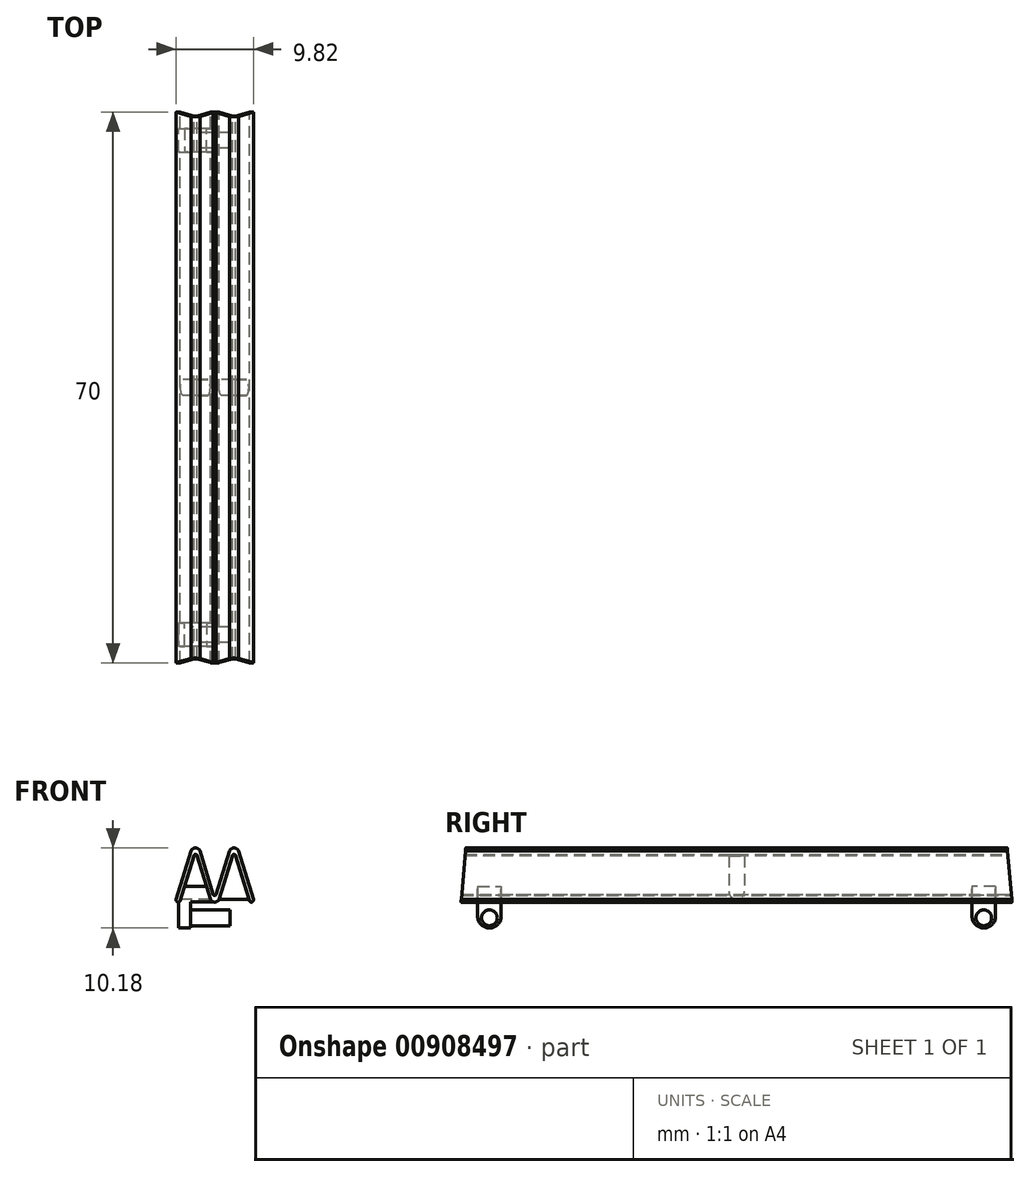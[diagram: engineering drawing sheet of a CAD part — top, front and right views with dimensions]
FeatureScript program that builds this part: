
annotation { "Feature Type Name" : "Feature", "Feature Type Description" : "" }
export const myFeature = defineFeature(function(context is Context, id is Id, definition is map)
    precondition{}
    {
        {
            var Q0;
            Q0=qCreatedBy(makeId("Front.planeOp"),FACE);
            var sketch = newSketch(context, id + "F0", { "sketchPlane" : qUnion([Q0])});
            skLineSegment(sketch, "E0.MirrorCS", {"start": v(6, 0) * mm, "end": v(-6, 0) * mm, "construction": true});
            skLineSegment(sketch, "E1", {"start": v(-6, 9.34) * mm, "end": v(-6, 0) * mm, "construction": true});
            skLineSegment(sketch, "E2", {"start": v(6, 9.34) * mm, "end": v(6, 0) * mm, "construction": true});
            skLineSegment(sketch, "E3", {"start": v(0.55, -1.05) * mm, "end": v(0.55, 2.53) * mm, "construction": true});
            skLineSegment(sketch, "E4", {"start": v(-6, 9.34) * mm, "end": v(6, 9.34) * mm, "construction": true});
            skPoint(sketch, "E5.visualSharp", {"position": v(-3, 9.34) * mm});
            skArc(sketch, "E5.filletArc", {"start": v(-1.89, 6.51) * mm, "mid": v(-2.45, 6.9) * mm, "end": v(-3, 6.51) * mm});
            skLineSegment(sketch, "E6", {"start": v(-2.45, 6.64) * mm, "end": v(-2.45, 7.24) * mm, "construction": true});
            skLineSegment(sketch, "E7", {"start": v(-3, 6.51) * mm, "end": v(-4.9, 0.34) * mm});
            skLineSegment(sketch, "E8.0", {"start": v(-2.63, 5.91) * mm, "end": v(-4.4, 0.2) * mm});
            skLineSegment(sketch, "E9.MirrorCS", {"start": v(-1.89, 6.51) * mm, "end": v(-0.19, 0.98) * mm});
            skLineSegment(sketch, "E10.MirrorCS", {"start": v(-2.26, 5.91) * mm, "end": v(-0.56, 0.38) * mm});
            skLineSegment(sketch, "E11", {"start": v(-4.5, 4.5) * mm, "end": v(6, 4.5) * mm, "construction": true});
            skPoint(sketch, "E11.endSnap0", {"position": v(-0.95, 3.45) * mm});
            skArc(sketch, "E12.MirrorCS", {"start": v(0.56, 0.38) * mm, "mid": v(0, 0) * mm, "end": v(-0.56, 0.38) * mm});
            skLineSegment(sketch, "E13", {"start": v(0, 0) * mm, "end": v(-6.05, 0) * mm, "construction": true});
            skArc(sketch, "E14", {"start": v(-4.9, 0.34) * mm, "mid": v(-4.72, 0.01) * mm, "end": v(-4.4, 0.2) * mm});
            skLineSegment(sketch, "E15", {"start": v(0, 0) * mm, "end": v(0, 2.5) * mm, "construction": true});
            skLineSegment(sketch, "E16.MirrorCS", {"start": v(1.89, 6.51) * mm, "end": v(0.19, 0.98) * mm});
            skLineSegment(sketch, "E17.MirrorCS", {"start": v(2.26, 5.91) * mm, "end": v(0.56, 0.38) * mm});
            skArc(sketch, "E18.MirrorCS", {"start": v(1.89, 6.51) * mm, "mid": v(2.45, 6.9) * mm, "end": v(3, 6.51) * mm});
            skLineSegment(sketch, "E19.MirrorCS", {"start": v(3, 6.51) * mm, "end": v(4.9, 0.34) * mm});
            skLineSegment(sketch, "E20.MirrorCS", {"start": v(2.63, 5.91) * mm, "end": v(4.4, 0.2) * mm});
            skArc(sketch, "E21.MirrorCS", {"start": v(4.9, 0.34) * mm, "mid": v(4.72, 0.01) * mm, "end": v(4.4, 0.2) * mm});
            skArc(sketch, "E22", {"start": v(-2.63, 5.91) * mm, "mid": v(-2.45, 6.06) * mm, "end": v(-2.26, 5.91) * mm});
            skArc(sketch, "E23", {"start": v(2.26, 5.91) * mm, "mid": v(2.45, 6.06) * mm, "end": v(2.63, 5.91) * mm});
            skArc(sketch, "E24.MirrorCS", {"start": v(-0.19, 0.98) * mm, "mid": v(0, 0.83) * mm, "end": v(0.19, 0.98) * mm});
            skSolve(sketch);
        }
        {
            var Q0;
            Q0=makeQuery(id+"F0.imprint","IMPRINT",FACE,{"disambiguationData":[TD([[makeQuery(id+"F0.imprint","IMPRINT",EDGE,{"derivedFrom":sQuery(id+"F0.wireOp",EDGE,"E5.filletArc")}),1.0]])]});
            extrude(context, id + "F1", {"entities" : qUnion([Q0]), "depth" : 70 * mm, "offsetDistance" : 25 * mm});
        }
        {
            var Q0;
            Q0=qCreatedBy(makeId("Top.planeOp"),FACE);
            var sketch = newSketch(context, id + "F2", { "sketchPlane" : qUnion([Q0])});
            skLineSegment(sketch, "E25", {"start": v(-4.9, -70) * mm, "end": v(-9.9, -70) * mm, "construction": true});
            skLineSegment(sketch, "E26.0", {"start": v(-4.9, -66.4) * mm, "end": v(-9.9, -66.4) * mm, "construction": true});
            skLineSegment(sketch, "E27", {"start": v(-4.9, 0) * mm, "end": v(-9.9, 0) * mm, "construction": true});
            skLineSegment(sketch, "E28.0", {"start": v(-4.9, -3.6) * mm, "end": v(-9.9, -3.6) * mm, "construction": true});
            skLineSegment(sketch, "E29", {"start": v(-9.9, -70) * mm, "end": v(-9.9, 0) * mm, "construction": true});
            skLineSegment(sketch, "E30", {"start": v(-9.9, -35) * mm, "end": v(10.62, -35) * mm, "construction": true});
            skSolve(sketch);
        }
        {
            var Q0;
            Q0=qCreatedBy(makeId("Right.planeOp"),FACE);
            cPlane(context, id + "F3", {"entities" : qUnion([Q0]), "cplaneType" : CPlaneType.OFFSET, "offset" : 2.45 * mm, "oppositeDirection" : true, "width" : 150 * mm, "height" : 150 * mm});
        }
        {
            var Q0;
            Q0=qCreatedBy(id+"F3.planeOp",FACE);
            var sketch = newSketch(context, id + "F4", { "sketchPlane" : qUnion([Q0])});
            skLineSegment(sketch, "E31", {"start": v(-67.9, 1.52) * mm, "end": v(-67.9, 0.01) * mm, "construction": true});
            skLineSegment(sketch, "E32.bottom", {"start": v(-67.9, 0.01) * mm, "end": v(-64.9, 0.01) * mm});
            skLineSegment(sketch, "E32.top", {"start": v(-67.9, 2.01) * mm, "end": v(-64.9, 2.01) * mm});
            skLineSegment(sketch, "E32.left", {"start": v(-67.9, 0.01) * mm, "end": v(-67.9, 2.01) * mm});
            skLineSegment(sketch, "E32.right", {"start": v(-64.9, 0.01) * mm, "end": v(-64.9, 2.01) * mm});
            skLineSegment(sketch, "E33", {"start": v(-35, -42.9) * mm, "end": v(-35, 0) * mm, "construction": true});
            skLineSegment(sketch, "E34.MirrorCS", {"start": v(-2.1, 0.01) * mm, "end": v(-5.1, 0.01) * mm});
            skLineSegment(sketch, "E35.MirrorCS", {"start": v(-2.1, 2.01) * mm, "end": v(-5.1, 2.01) * mm});
            skLineSegment(sketch, "E36.MirrorCS", {"start": v(-5.1, 0.01) * mm, "end": v(-5.1, 2.01) * mm});
            skLineSegment(sketch, "E37.MirrorCS", {"start": v(-2.1, 0.01) * mm, "end": v(-2.1, 2.01) * mm});
            skSolve(sketch);
        }
        {
            var Q0;
            Q0=makeQuery(id+"F4.imprint","IMPRINT",FACE,{"disambiguationData":[TD([[makeQuery(id+"F4.imprint","IMPRINT",EDGE,{"derivedFrom":sQuery(id+"F4.wireOp",EDGE,"E32.bottom")}),1.0]])]});
            var Q1;
            Q1=makeQuery(id+"F1.opExtrude","SWEPT_FACE",FACE,{"disambiguationData":[OSD([sQuery(id+"F0.wireOp",EDGE,"E9.MirrorCS")])]});
            extrude(context, id + "F5", {"entities" : qUnion([Q0]), "operationType" : NewBodyOperationType.ADD, "endBound" : BoundingType.UP_TO_SURFACE, "depth" : 25 * mm, "endBoundEntityFace" : qUnion([Q1]), "offsetDistance" : 25 * mm});
        }
        {
            var Q0;
            Q0=makeQuery(id+"F5.opExtrude","CAP_FACE",FACE,{"disambiguationData":[OSD([sQuery(id+"F4.wireOp",EDGE,"E32.bottom"),sQuery(id+"F4.wireOp",EDGE,"E32.top"),sQuery(id+"F4.wireOp",EDGE,"E32.left"),sQuery(id+"F4.wireOp",EDGE,"E32.right")])],"isStart":true});
            var Q1;
            Q1=makeQuery(id+"F1.opExtrude","SWEPT_FACE",FACE,{"disambiguationData":[OSD([sQuery(id+"F0.wireOp",EDGE,"E8.0")])]});
            extrude(context, id + "F6", {"entities" : qUnion([Q0]), "operationType" : NewBodyOperationType.ADD, "endBound" : BoundingType.UP_TO_SURFACE, "depth" : 25 * mm, "endBoundEntityFace" : qUnion([Q1]), "hasOffset" : true, "offsetDistance" : -0.2 * mm});
        }
        {
            var Q0;
            {var subQ0=sQuery(id+"F4.wireOp",EDGE,"E32.bottom");Q0=makeQuery(id+"F6.boolean.opBoolean","MERGE",FACE,{"derivedFrom":[makeQuery(id+"F5.opExtrude","SWEPT_FACE",FACE,{"disambiguationData":[OSD([subQ0])]}),makeQuery(id+"F6.opExtrude","SWEPT_FACE",FACE,{"disambiguationData":[OSD([subQ0])]})]});}
            var sketch = newSketch(context, id + "F7", { "sketchPlane" : qUnion([Q0])});
            skLineSegment(sketch, "E38", {"start": v(-4.57, 66.4) * mm, "end": v(-0.11, 66.4) * mm, "construction": true});
            skLineSegment(sketch, "E39", {"start": v(-4.57, 69) * mm, "end": v(-4.57, 63.84) * mm, "construction": true});
            skLineSegment(sketch, "E40.bottom", {"start": v(-4.57, 64.9) * mm, "end": v(-3.07, 64.9) * mm});
            skLineSegment(sketch, "E40.top", {"start": v(-4.57, 67.9) * mm, "end": v(-3.07, 67.9) * mm});
            skLineSegment(sketch, "E40.left", {"start": v(-4.57, 64.9) * mm, "end": v(-4.57, 67.9) * mm});
            skLineSegment(sketch, "E40.right", {"start": v(-3.07, 64.9) * mm, "end": v(-3.07, 67.9) * mm});
            skPoint(sketch, "E40.middle", {"position": v(-3.82, 66.4) * mm});
            skLineSegment(sketch, "E41", {"start": v(-26.98, 35) * mm, "end": v(-9.9, 35) * mm, "construction": true});
            skLineSegment(sketch, "E42.MirrorCS", {"start": v(-4.57, 1) * mm, "end": v(-4.57, 6.16) * mm, "construction": true});
            skLineSegment(sketch, "E43.MirrorCS", {"start": v(-4.57, 5.1) * mm, "end": v(-3.07, 5.1) * mm});
            skLineSegment(sketch, "E44.MirrorCS", {"start": v(-4.57, 5.1) * mm, "end": v(-4.57, 2.1) * mm});
            skLineSegment(sketch, "E45.MirrorCS", {"start": v(-4.57, 2.1) * mm, "end": v(-3.07, 2.1) * mm});
            skLineSegment(sketch, "E46.MirrorCS", {"start": v(-3.07, 5.1) * mm, "end": v(-3.07, 2.1) * mm});
            skPoint(sketch, "E47.MirrorP", {"position": v(-3.82, 3.6) * mm});
            skSolve(sketch);
        }
        {
            var Q0;
            Q0=makeQuery(id+"F7.imprint","IMPRINT",FACE,{"disambiguationData":[TD([[makeQuery(id+"F7.imprint","IMPRINT",EDGE,{"derivedFrom":sQuery(id+"F7.wireOp",EDGE,"E40.bottom")}),-1.0]])]});
            extrude(context, id + "F8", {"entities" : qUnion([Q0]), "operationType" : NewBodyOperationType.ADD, "depth" : 3.3 * mm, "offsetDistance" : 25 * mm});
        }
        {
            var Q0;
            Q0=makeQuery(id+"F8.opExtrude","CAP_EDGE",EDGE,{"disambiguationData":[OSD([sQuery(id+"F7.wireOp",EDGE,"E40.top")])],"isStart":false});
            var Q1;
            Q1=makeQuery(id+"F8.opExtrude","CAP_EDGE",EDGE,{"disambiguationData":[OSD([sQuery(id+"F7.wireOp",EDGE,"E40.bottom")])],"isStart":false});
            fillet(context, id + "F9", {"entities" : qUnion([Q0, Q1]), "radius" : 1.5 * mm, "tangentPropagation" : true, "allowEdgeOverflow" : false});
        }
        {
            var Q0;
            Q0=makeQuery(id+"F8.opExtrude","SWEPT_FACE",FACE,{"disambiguationData":[OSD([sQuery(id+"F7.wireOp",EDGE,"E40.right")])]});
            var sketch = newSketch(context, id + "F10", { "sketchPlane" : qUnion([Q0])});
            skLineSegment(sketch, "E48", {"start": v(-66.4, 0.01) * mm, "end": v(-66.4, -1.99) * mm, "construction": true});
            skCircle(sketch, "E49", {"center": v(-66.4, -1.99) * mm, "radius": 1 * mm});
            skSolve(sketch);
        }
        {
            var Q0;
            Q0=qSketchRegion(id+"F10",true);
            extrude(context, id + "F11", {"entities" : qUnion([Q0]), "operationType" : NewBodyOperationType.ADD, "depth" : 5 * mm, "offsetDistance" : 25 * mm});
        }
        {
            var Q0;
            Q0=makeQuery(id+"F4.imprint","IMPRINT",FACE,{"disambiguationData":[TD([[makeQuery(id+"F4.imprint","IMPRINT",EDGE,{"derivedFrom":sQuery(id+"F4.wireOp",EDGE,"E34.MirrorCS")}),-1.0]])]});
            var Q1;
            Q1=makeQuery(id+"F5.boolean.opBoolean","MERGE",FACE,{"derivedFrom":[makeQuery(id+"F1.opExtrude","SWEPT_FACE",FACE,{"disambiguationData":[OSD([sQuery(id+"F0.wireOp",EDGE,"E9.MirrorCS")])]}),makeQuery(id+"F5.opExtrude","CAP_FACE",FACE,{"disambiguationData":[OSD([sQuery(id+"F4.wireOp",EDGE,"E32.bottom"),sQuery(id+"F4.wireOp",EDGE,"E32.top"),sQuery(id+"F4.wireOp",EDGE,"E32.left"),sQuery(id+"F4.wireOp",EDGE,"E32.right")])],"isStart":false})]});
            extrude(context, id + "F12", {"entities" : qUnion([Q0]), "operationType" : NewBodyOperationType.ADD, "endBound" : BoundingType.UP_TO_SURFACE, "depth" : 25 * mm, "endBoundEntityFace" : qUnion([Q1]), "offsetDistance" : 25 * mm});
        }
        {
            var Q0;
            Q0=makeQuery(id+"F4.imprint","IMPRINT",FACE,{"disambiguationData":[TD([[makeQuery(id+"F4.imprint","IMPRINT",EDGE,{"derivedFrom":sQuery(id+"F4.wireOp",EDGE,"E34.MirrorCS")}),-1.0]])]});
            var Q1;
            Q1=makeQuery(id+"F1.opExtrude","SWEPT_FACE",FACE,{"disambiguationData":[OSD([sQuery(id+"F0.wireOp",EDGE,"E8.0")])]});
            extrude(context, id + "F13", {"entities" : qUnion([Q0]), "operationType" : NewBodyOperationType.ADD, "endBound" : BoundingType.UP_TO_SURFACE, "oppositeDirection" : true, "depth" : 25 * mm, "endBoundEntityFace" : qUnion([Q1]), "hasOffset" : true, "offsetDistance" : -0.2 * mm});
        }
        {
            var Q0;
            Q0=makeQuery(id+"F7.imprint","IMPRINT",FACE,{"disambiguationData":[TD([[makeQuery(id+"F7.imprint","IMPRINT",EDGE,{"derivedFrom":sQuery(id+"F7.wireOp",EDGE,"E43.MirrorCS")}),-1.0]])]});
            extrude(context, id + "F14", {"entities" : qUnion([Q0]), "operationType" : NewBodyOperationType.ADD, "depth" : 3.3 * mm, "offsetDistance" : 25 * mm});
        }
        {
            var Q0;
            Q0=makeQuery(id+"F14.opExtrude","CAP_EDGE",EDGE,{"disambiguationData":[OSD([sQuery(id+"F7.wireOp",EDGE,"E45.MirrorCS")])],"isStart":false});
            var Q1;
            Q1=makeQuery(id+"F14.opExtrude","CAP_EDGE",EDGE,{"disambiguationData":[OSD([sQuery(id+"F7.wireOp",EDGE,"E43.MirrorCS")])],"isStart":false});
            fillet(context, id + "F15", {"entities" : qUnion([Q0, Q1]), "radius" : 1.5 * mm, "tangentPropagation" : true, "allowEdgeOverflow" : false});
        }
        {
            var Q0;
            Q0=makeQuery(id+"F14.opExtrude","SWEPT_FACE",FACE,{"disambiguationData":[OSD([sQuery(id+"F7.wireOp",EDGE,"E46.MirrorCS")])]});
            var sketch = newSketch(context, id + "F16", { "sketchPlane" : qUnion([Q0])});
            skLineSegment(sketch, "E50", {"start": v(-3.6, 0.01) * mm, "end": v(-3.6, -1.99) * mm, "construction": true});
            skCircle(sketch, "E51", {"center": v(-3.6, -1.99) * mm, "radius": 1 * mm});
            skSolve(sketch);
        }
        {
            var Q0;
            Q0=makeQuery(id+"F16.imprint","IMPRINT",FACE,{"disambiguationData":[TD([[makeQuery(id+"F16.imprint","IMPRINT",EDGE,{"derivedFrom":sQuery(id+"F16.wireOp",EDGE,"E51")}),1.0]])]});
            extrude(context, id + "F17", {"entities" : qUnion([Q0]), "operationType" : NewBodyOperationType.ADD, "depth" : 5 * mm, "offsetDistance" : 25 * mm});
        }
        {
            var Q0;
            Q0=qCreatedBy(makeId("Right.planeOp"),FACE);
            var sketch = newSketch(context, id + "F18", { "sketchPlane" : qUnion([Q0])});
            skLineSegment(sketch, "E52", {"start": v(-70, 0) * mm, "end": v(-70, -4.12) * mm, "construction": true});
            skLineSegment(sketch, "E53", {"start": v(-70, 0) * mm, "end": v(-69.2, 9.12) * mm});
            skLineSegment(sketch, "E54", {"start": v(-69.2, 9.12) * mm, "end": v(-70, 9.12) * mm});
            skLineSegment(sketch, "E55", {"start": v(-70, 9.12) * mm, "end": v(-70, 0) * mm});
            skLineSegment(sketch, "E56", {"start": v(-35, 0) * mm, "end": v(-35, 8.82) * mm, "construction": true});
            skLineSegment(sketch, "E57.MirrorCS", {"start": v(-0.8, 9.12) * mm, "end": v(0, 9.12) * mm});
            skLineSegment(sketch, "E58.MirrorCS", {"start": v(0, 0) * mm, "end": v(-0.8, 9.12) * mm});
            skLineSegment(sketch, "E59.MirrorCS", {"start": v(0, 9.12) * mm, "end": v(0, 0) * mm});
            skLineSegment(sketch, "E60.MirrorCS", {"start": v(0, 0) * mm, "end": v(0, -4.12) * mm, "construction": true});
            skSolve(sketch);
        }
        {
            var Q0;
            Q0=qSketchRegion(id+"F18",true);
            extrude(context, id + "F19", {"entities" : qUnion([Q0]), "operationType" : NewBodyOperationType.REMOVE, "endBound" : BoundingType.SYMMETRIC, "oppositeDirection" : true, "depth" : 25 * mm, "offsetDistance" : 25 * mm});
        }
        {
            var Q0;
            Q0=qCreatedBy(makeId("Front.planeOp"),FACE);
            cPlane(context, id + "F20", {"entities" : qUnion([Q0]), "cplaneType" : CPlaneType.OFFSET, "offset" : 35 * mm, "width" : 150 * mm, "height" : 150 * mm});
        }
        {
            var Q0;
            Q0=qCreatedBy(id+"F20.planeOp",FACE);
            var sketch = newSketch(context, id + "F21", { "sketchPlane" : qUnion([Q0])});
            skLineSegment(sketch, "E61", {"start": v(-2.45, 6.06) * mm, "end": v(-2.45, 10.06) * mm, "construction": true});
            skLineSegment(sketch, "E62", {"start": v(2.45, 6.06) * mm, "end": v(2.45, 10.06) * mm, "construction": true});
            skLineSegment(sketch, "E63.0", {"start": v(2.26, 5.9) * mm, "end": v(0.56, 0.38) * mm});
            skLineSegment(sketch, "E64.MirrorCS", {"start": v(2.63, 5.9) * mm, "end": v(4.33, 0.38) * mm});
            skArc(sketch, "E65", {"start": v(2.26, 5.9) * mm, "mid": v(2.45, 6.06) * mm, "end": v(2.63, 5.9) * mm});
            skLineSegment(sketch, "E66", {"start": v(4.33, 0.38) * mm, "end": v(0.56, 0.38) * mm});
            skLineSegment(sketch, "E67.0", {"start": v(-2.63, 5.9) * mm, "end": v(-4.33, 0.38) * mm});
            skLineSegment(sketch, "E68.MirrorCS", {"start": v(-2.26, 5.9) * mm, "end": v(-0.56, 0.38) * mm});
            skArc(sketch, "E69", {"start": v(-2.63, 5.9) * mm, "mid": v(-2.45, 6.06) * mm, "end": v(-2.26, 5.9) * mm});
            skLineSegment(sketch, "E70", {"start": v(-0.56, 0.38) * mm, "end": v(-4.33, 0.38) * mm});
            skSolve(sketch);
        }
        {
            var Q0;
            Q0 = qSketchRegion(id + "F21", true);
            extrude(context, id + "F22", {"entities" : qUnion([Q0]), "operationType" : NewBodyOperationType.ADD, "endBound" : BoundingType.SYMMETRIC, "depth" : 2 * mm, "offsetDistance" : 25 * mm});
        }
        {
            var Q0;
            Q0=makeQuery(id+"F22.opExtrude","CAP_EDGE",EDGE,{"disambiguationData":[OSD([sQuery(id+"F21.wireOp",EDGE,"E66")])],"isStart":false});
            var Q1;
            Q1=makeQuery(id+"F22.opExtrude","CAP_EDGE",EDGE,{"disambiguationData":[OSD([sQuery(id+"F21.wireOp",EDGE,"E70")])],"isStart":false});
            var Q2;
            Q2=makeQuery(id+"F22.opExtrude","CAP_EDGE",EDGE,{"disambiguationData":[OSD([sQuery(id+"F21.wireOp",EDGE,"E70")])],"isStart":true});
            var Q3;
            Q3=makeQuery(id+"F22.opExtrude","CAP_EDGE",EDGE,{"disambiguationData":[OSD([sQuery(id+"F21.wireOp",EDGE,"E66")])],"isStart":true});
            fillet(context, id + "F23", {"entities" : qUnion([Q0, Q1, Q2, Q3]), "radius" : 1 * mm, "tangentPropagation" : true, "allowEdgeOverflow" : false});
        }
    });
